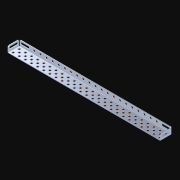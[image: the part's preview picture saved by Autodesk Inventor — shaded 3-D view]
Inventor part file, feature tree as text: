
AUTODESK INVENTOR PART (.ipt)
format: ipt  version: 2021 (Build 250183000, 183)  size: 1,430,016 bytes
history: native  units: in
note: dims shown in document units (in); Inventor stores cm internally (conversion verified against a paired STEP export)
features: other x96, extrude x95, pattern_linear x3, imported_body x1
ambient origin geometry x8: Origin, YZ Plane, XZ Plane, XY Plane, X Axis, Y Axis, Z Axis, Center Point
bodies: Body1 (feature_tree), Body2 (feature_tree), Body3 (feature_tree), Body4 (feature_tree), Body5 (feature_tree), Body6 (feature_tree), Body7 (feature_tree), Body8 (feature_tree), Body9 (feature_tree), Body10 (feature_tree), Body11 (feature_tree), Body12 (feature_tree), Body13 (feature_tree), Body14 (feature_tree), Body15 (feature_tree), Body16 (feature_tree), Body17 (feature_tree), Body18 (feature_tree), Body19 (feature_tree), Body20 (feature_tree), Body21 (feature_tree), Body22 (feature_tree), Body23 (feature_tree), Body24 (feature_tree), Body25 (feature_tree), Body26 (feature_tree), Body27 (feature_tree), Body28 (feature_tree), Body29 (feature_tree), Body30 (feature_tree), Body31 (feature_tree), Body32 (feature_tree), Body33 (feature_tree), Body34 (feature_tree), Body35 (feature_tree), Body36 (feature_tree), Body37 (feature_tree), Body38 (feature_tree), Body39 (feature_tree), Body40 (feature_tree), Body41 (feature_tree), Body42 (feature_tree), Body43 (feature_tree), Body44 (feature_tree), Body45 (feature_tree), Body46 (feature_tree), Body47 (feature_tree), Body48 (feature_tree), Body49 (feature_tree), Body50 (feature_tree), Body51 (feature_tree), Body52 (feature_tree), Body53 (feature_tree), Body54 (feature_tree), Body55 (feature_tree), Body56 (feature_tree), Body57 (feature_tree), Body58 (feature_tree), Body59 (feature_tree), Body60 (feature_tree), Body61 (feature_tree), Body62 (feature_tree), Body63 (feature_tree), Body64 (feature_tree), Body65 (feature_tree), Body66 (feature_tree), Body67 (feature_tree), Body68 (feature_tree), Body69 (feature_tree), Body70 (feature_tree), Body71 (feature_tree), Body72 (feature_tree), Body73 (feature_tree), Body74 (feature_tree), Body75 (feature_tree), Body76 (feature_tree), Body77 (feature_tree), Body78 (feature_tree), Body79 (feature_tree), Body80 (feature_tree), Body81 (feature_tree), Body82 (feature_tree), Body83 (feature_tree), Body84 (feature_tree), Body85 (feature_tree), Body86 (feature_tree), Body87 (feature_tree), Body88 (feature_tree), Body89 (feature_tree), Body90 (feature_tree), Body91 (feature_tree), Body92 (feature_tree), Body93 (feature_tree), Body94 (feature_tree), Body95 (feature_tree), Body96 (feature_tree)
feature tree (195):
  parser-record x1  (decoder bookkeeping rows leaked as tree rows — omitted from the tree; the rows remain in map.json)
  imported_body  "Base1"
  pattern_linear  "Rectangular Pattern1"  Spacing1=0.046in  [1 undecoded]
  pattern_linear  "Rectangular Pattern2"  Count1=25 Spacing1=0.5in
  pattern_linear  "Rectangular Pattern3"  Count1=2 Spacing1=0.5in
  other  "Srf1"
  other  "Srf2"
  other  "Srf3"
  other  "Srf4"
  other  "Srf5"
  other  "Srf6"
  other  "Srf7"
  other  "Srf8"
  other  "Srf9"
  other  "Srf10"
  other  "Srf11"
  other  "Srf12"
  other  "Srf13"
  other  "Srf14"
  other  "Srf15"
  other  "Srf16"
  other  "Srf17"
  other  "Srf18"
  other  "Srf19"
  other  "Srf20"
  other  "Srf21"
  other  "Srf22"
  other  "Srf23"
  other  "Srf24"
  other  "Srf25"
  other  "Srf26"
  other  "Srf27"
  other  "Srf28"
  other  "Srf29"
  other  "Srf30"
  other  "Srf31"
  other  "Srf32"
  other  "Srf33"
  other  "Srf34"
  other  "Srf35"
  other  "Srf36"
  other  "Srf37"
  other  "Srf38"
  other  "Srf39"
  other  "Srf40"
  other  "Srf41"
  other  "Srf42"
  other  "Srf43"
  other  "Srf44"
  other  "Srf45"
  other  "Srf46"
  other  "Srf47"
  other  "Srf48"
  other  "Srf49"
  other  "Srf50"
  other  "Srf51"
  other  "Srf52"
  other  "Srf53"
  other  "Srf54"
  other  "Srf55"
  other  "Srf56"
  other  "Srf57"
  other  "Srf58"
  other  "Srf59"
  other  "Srf60"
  other  "Srf61"
  other  "Srf62"
  other  "Srf63"
  other  "Srf64"
  other  "Srf65"
  other  "Srf66"
  other  "Srf67"
  other  "Srf68"
  other  "Srf69"
  other  "Srf70"
  other  "Srf71"
  other  "Srf72"
  other  "Srf73"
  other  "Srf74"
  other  "Srf75"
  other  "Srf76"
  other  "Srf77"
  other  "Srf78"
  other  "Srf79"
  other  "Srf80"
  other  "Srf81"
  other  "Srf82"
  other  "Srf83"
  other  "Srf84"
  other  "Srf85"
  other  "Srf86"
  other  "Srf87"
  other  "Srf88"
  other  "Srf89"
  other  "Srf90"
  other  "Srf91"
  other  "Srf92"
  other  "Srf93"
  other  "Srf94"
  other  "Srf95"
  extrude  "ExtrusionSrf1"  Depth=0.046in TaperAngle=0.0deg
  extrude  "ExtrusionSrf51"  Depth=0.5in
  extrude  "ExtrusionSrf75"  Depth=0.046in TaperAngle=0.0deg
  extrude  "ExtrusionSrf2"  Depth=0.5in
  extrude  "ExtrusionSrf3"  [1 undecoded]
  extrude  "ExtrusionSrf4"  [1 undecoded]
  extrude  "ExtrusionSrf5"  [1 undecoded]
  extrude  "ExtrusionSrf6"  [1 undecoded]
  extrude  "ExtrusionSrf7"  [1 undecoded]
  extrude  "ExtrusionSrf8"  [1 undecoded]
  extrude  "ExtrusionSrf9"  [1 undecoded]
  extrude  "ExtrusionSrf10"  [1 undecoded]
  extrude  "ExtrusionSrf11"  [1 undecoded]
  extrude  "ExtrusionSrf12"  [1 undecoded]
  extrude  "ExtrusionSrf13"  [1 undecoded]
  extrude  "ExtrusionSrf14"  [1 undecoded]
  extrude  "ExtrusionSrf15"  [1 undecoded]
  extrude  "ExtrusionSrf16"  [1 undecoded]
  extrude  "ExtrusionSrf17"  [1 undecoded]
  extrude  "ExtrusionSrf18"  [1 undecoded]
  extrude  "ExtrusionSrf19"  [1 undecoded]
  extrude  "ExtrusionSrf20"  [1 undecoded]
  extrude  "ExtrusionSrf21"  [1 undecoded]
  extrude  "ExtrusionSrf22"  [1 undecoded]
  extrude  "ExtrusionSrf23"  [1 undecoded]
  extrude  "ExtrusionSrf24"  [1 undecoded]
  extrude  "ExtrusionSrf25"  [1 undecoded]
  extrude  "ExtrusionSrf26"  [1 undecoded]
  extrude  "ExtrusionSrf27"  [1 undecoded]
  extrude  "ExtrusionSrf28"  [1 undecoded]
  extrude  "ExtrusionSrf29"  [1 undecoded]
  extrude  "ExtrusionSrf30"  [1 undecoded]
  extrude  "ExtrusionSrf31"  [1 undecoded]
  extrude  "ExtrusionSrf32"  [1 undecoded]
  extrude  "ExtrusionSrf33"  [1 undecoded]
  extrude  "ExtrusionSrf34"  [1 undecoded]
  extrude  "ExtrusionSrf35"  [1 undecoded]
  extrude  "ExtrusionSrf36"  [1 undecoded]
  extrude  "ExtrusionSrf37"  [1 undecoded]
  extrude  "ExtrusionSrf38"  [1 undecoded]
  extrude  "ExtrusionSrf39"  [1 undecoded]
  extrude  "ExtrusionSrf40"  [1 undecoded]
  extrude  "ExtrusionSrf41"  [1 undecoded]
  extrude  "ExtrusionSrf42"  [1 undecoded]
  extrude  "ExtrusionSrf43"  [1 undecoded]
  extrude  "ExtrusionSrf44"  [1 undecoded]
  extrude  "ExtrusionSrf45"  [1 undecoded]
  extrude  "ExtrusionSrf46"  [1 undecoded]
  extrude  "ExtrusionSrf47"  [1 undecoded]
  extrude  "ExtrusionSrf48"  [1 undecoded]
  extrude  "ExtrusionSrf49"  [1 undecoded]
  extrude  "ExtrusionSrf50"  [1 undecoded]
  extrude  "ExtrusionSrf52"  [1 undecoded]
  extrude  "ExtrusionSrf53"  [1 undecoded]
  extrude  "ExtrusionSrf54"  [1 undecoded]
  extrude  "ExtrusionSrf55"  [1 undecoded]
  extrude  "ExtrusionSrf56"  [1 undecoded]
  extrude  "ExtrusionSrf57"  [1 undecoded]
  extrude  "ExtrusionSrf58"  [1 undecoded]
  extrude  "ExtrusionSrf59"  [1 undecoded]
  extrude  "ExtrusionSrf60"  [1 undecoded]
  extrude  "ExtrusionSrf61"  [1 undecoded]
  extrude  "ExtrusionSrf62"  [1 undecoded]
  extrude  "ExtrusionSrf63"  [1 undecoded]
  extrude  "ExtrusionSrf64"  [1 undecoded]
  extrude  "ExtrusionSrf65"  [1 undecoded]
  extrude  "ExtrusionSrf66"  [1 undecoded]
  extrude  "ExtrusionSrf67"  [1 undecoded]
  extrude  "ExtrusionSrf68"  [1 undecoded]
  extrude  "ExtrusionSrf69"  [1 undecoded]
  extrude  "ExtrusionSrf70"  [1 undecoded]
  extrude  "ExtrusionSrf71"  [1 undecoded]
  extrude  "ExtrusionSrf72"  [1 undecoded]
  extrude  "ExtrusionSrf73"  [1 undecoded]
  extrude  "ExtrusionSrf74"  [1 undecoded]
  extrude  "ExtrusionSrf76"  [1 undecoded]
  extrude  "ExtrusionSrf77"  [1 undecoded]
  extrude  "ExtrusionSrf78"  [1 undecoded]
  extrude  "ExtrusionSrf79"  [1 undecoded]
  extrude  "ExtrusionSrf80"  [1 undecoded]
  extrude  "ExtrusionSrf81"  [1 undecoded]
  extrude  "ExtrusionSrf82"  [1 undecoded]
  extrude  "ExtrusionSrf83"  [1 undecoded]
  extrude  "ExtrusionSrf84"  [1 undecoded]
  extrude  "ExtrusionSrf85"  [1 undecoded]
  extrude  "ExtrusionSrf86"  [1 undecoded]
  extrude  "ExtrusionSrf87"  [1 undecoded]
  extrude  "ExtrusionSrf88"  [1 undecoded]
  extrude  "ExtrusionSrf89"  [1 undecoded]
  extrude  "ExtrusionSrf90"  [1 undecoded]
  extrude  "ExtrusionSrf91"  [1 undecoded]
  extrude  "ExtrusionSrf92"  [1 undecoded]
  extrude  "ExtrusionSrf93"  [1 undecoded]
  extrude  "ExtrusionSrf94"  [1 undecoded]
  extrude  "ExtrusionSrf95"  [1 undecoded]
note: 92 required parameter values undecoded (feature->parameter linkage not recoverable at this tier; creation-order binding heuristic only, values carry confidence <= 0.55)
